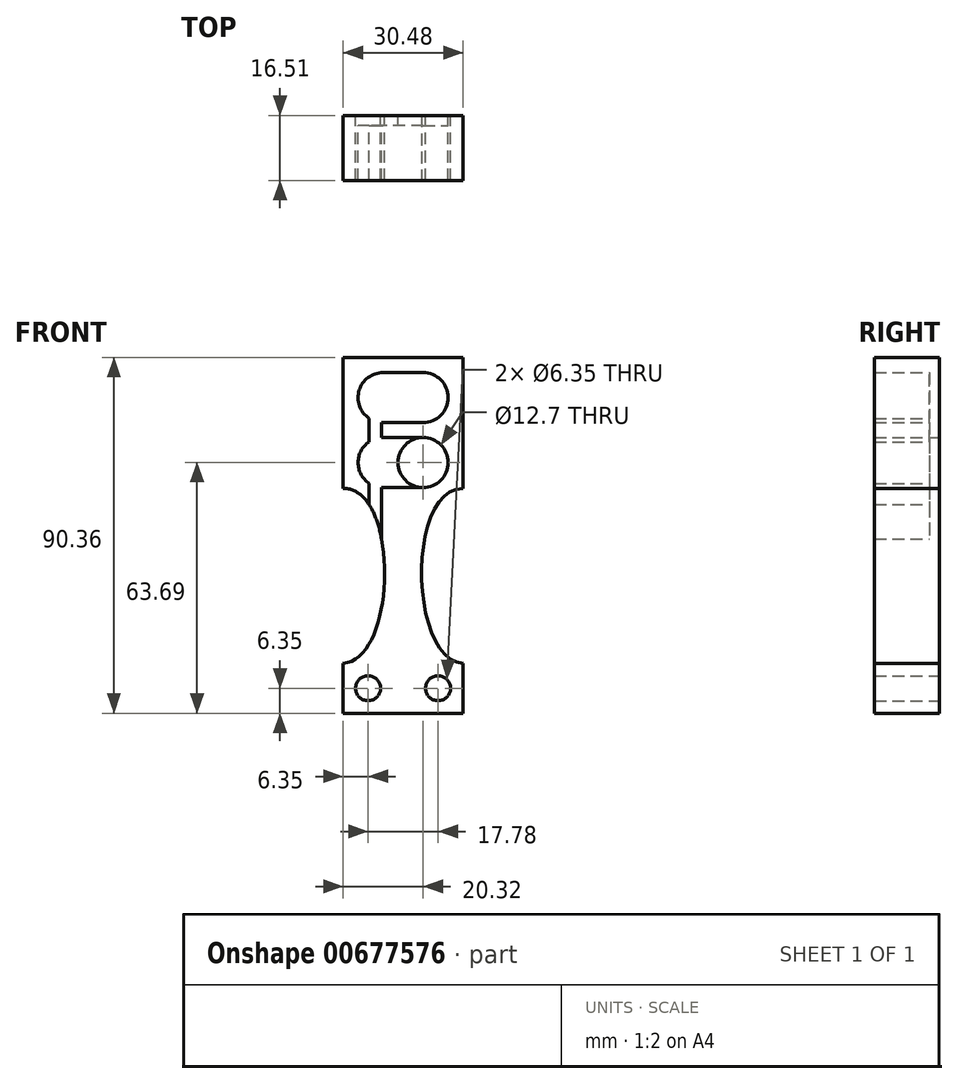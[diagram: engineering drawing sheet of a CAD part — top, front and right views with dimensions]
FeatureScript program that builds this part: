
annotation { "Feature Type Name" : "Feature", "Feature Type Description" : "" }
export const myFeature = defineFeature(function(context is Context, id is Id, definition is map)
    precondition{}
    {
        {
            var Q0;
            Q0=qCreatedBy(makeId("Front.planeOp"),FACE);
            var sketch = newSketch(context, id + "F0", { "sketchPlane" : qUnion([Q0])});
            skLineSegment(sketch, "E0", {"start": v(0, 10.16) * mm, "end": v(15.24, 10.16) * mm});
            skLineSegment(sketch, "E1", {"start": v(15.24, 10.16) * mm, "end": v(15.24, -23.05) * mm});
            skLineSegment(sketch, "E2", {"start": v(37.3, -67.5) * mm, "end": v(37.3, -80.2) * mm});
            skLineSegment(sketch, "E3", {"start": v(37.3, -80.2) * mm, "end": v(0, -80.2) * mm});
            skLineSegment(sketch, "E4.MirrorCS", {"start": v(-15.24, 10.16) * mm, "end": v(-15.24, -23.05) * mm});
            skLineSegment(sketch, "E5.MirrorCS", {"start": v(-37.3, -67.5) * mm, "end": v(-37.3, -80.2) * mm});
            skLineSegment(sketch, "E6.MirrorCS", {"start": v(0, 10.16) * mm, "end": v(-15.24, 10.16) * mm});
            skLineSegment(sketch, "E7.MirrorCS", {"start": v(-37.3, -80.2) * mm, "end": v(0, -80.2) * mm});
            skLineSegment(sketch, "E8", {"start": v(-37.3, -67.5) * mm, "end": v(-15.24, -67.5) * mm});
            skLineSegment(sketch, "E9.MirrorCS", {"start": v(37.3, -67.5) * mm, "end": v(15.24, -67.5) * mm});
            skCircle(sketch, "E10", {"center": v(5.08, 0) * mm, "radius": 6.35 * mm});
            skCircle(sketch, "E11.MirrorC", {"center": v(-5.08, 0) * mm, "radius": 6.35 * mm});
            skLineSegment(sketch, "E12", {"start": v(5.08, 6.35) * mm, "end": v(-5.08, 6.35) * mm});
            skLineSegment(sketch, "E13", {"start": v(-5.08, -6.35) * mm, "end": v(5.08, -6.35) * mm});
            skFitSpline(sketch, "E14", {"points": [v(-15.24, -23.05) * mm, v(-15.24, -67.5) * mm], "startDerivative": vector(43.33, 0) * mm, "endDerivative": vector(-41, -2.46) * mm});
            skFitSpline(sketch, "E15.MirrorCS", {"points": [v(15.24, -23.05) * mm, v(15.24, -67.5) * mm], "startDerivative": vector(-43.33, 0) * mm, "endDerivative": vector(41, -2.46) * mm});
            skCircle(sketch, "E16", {"center": v(-5.08, -16.51) * mm, "radius": 6.35 * mm});
            skCircle(sketch, "E17.MirrorC", {"center": v(5.08, -16.51) * mm, "radius": 6.35 * mm});
            skLineSegment(sketch, "E18", {"start": v(5.08, -10.16) * mm, "end": v(-5.08, -10.16) * mm});
            skLineSegment(sketch, "E19", {"start": v(5.08, -22.86) * mm, "end": v(-5.08, -22.86) * mm});
            skPoint(sketch, "E20", {"position": v(0, -16.51) * mm});
            skLineSegment(sketch, "E21", {"start": v(-8.64, -21.77) * mm, "end": v(-8.64, -27.19) * mm});
            skLineSegment(sketch, "E22", {"start": v(-5.46, -6.34) * mm, "end": v(-5.46, -10.17) * mm});
            skLineSegment(sketch, "E23", {"start": v(-5.46, -10.17) * mm, "end": v(-5.46, -22.6) * mm});
            skLineSegment(sketch, "E24", {"start": v(-5.46, -22.6) * mm, "end": v(-5.46, -35.93) * mm});
            skLineSegment(sketch, "E25", {"start": v(-15.24, -67.5) * mm, "end": v(-15.24, -80.2) * mm});
            skPoint(sketch, "E25.endSnap0", {"position": v(-18.65, -80.2) * mm});
            skLineSegment(sketch, "E26", {"start": v(15.24, -67.5) * mm, "end": v(15.24, -80.2) * mm});
            skLineSegment(sketch, "E27", {"start": v(-8.64, -11.25) * mm, "end": v(-8.64, -5.26) * mm});
            skCircle(sketch, "E28", {"center": v(8.89, -73.85) * mm, "radius": 3.18 * mm});
            skCircle(sketch, "E29.MirrorC", {"center": v(-8.89, -73.85) * mm, "radius": 3.18 * mm});
            skSolve(sketch);
        }
        {
            var Q0;
            Q0=makeQuery(id+"F0.imprint","IMPRINT",FACE,{"disambiguationData":[TD([[makeQuery(id+"F0.imprint","IMPRINT",EDGE,{"derivedFrom":sQuery(id+"F0.wireOp",EDGE,"E0")}),-1.0]])]});
            extrude(context, id + "F1", {"entities" : qUnion([Q0]), "depth" : 16.5 * mm, "offsetDistance" : 25.4 * mm});
        }
        {
            var Q0;
            {var subQ0=sQuery(id+"F0.wireOp",EDGE,"E11.MirrorC");var subQ2=sQuery(id+"F0.wireOp",EDGE,"E10");var subQ5=makeQuery(id+"F0.imprint","INTERSECT",VERTEX,{"disambiguationData":[OD(0.0)],"derivedFrom":[subQ2,subQ0]});Q0=makeQuery(id+"F0.imprint","IMPRINT",FACE,{"disambiguationData":[TD([[makeQuery(id+"F0.imprint","IMPRINT",EDGE,{"disambiguationData":[TD([[subQ5,-1.0]])],"derivedFrom":subQ2}),-1.0]])]});}
            var Q1;
            {var subQ0=sQuery(id+"F0.wireOp",EDGE,"E10");var subQ1=makeQuery(id+"F0.imprint","INTERSECT",VERTEX,{"derivedFrom":[subQ0,sQuery(id+"F0.wireOp",EDGE,"E12")]});Q1=makeQuery(id+"F0.imprint","IMPRINT",FACE,{"disambiguationData":[TD([[makeQuery(id+"F0.imprint","IMPRINT",EDGE,{"disambiguationData":[TD([[subQ1,-1.0]])],"derivedFrom":subQ0}),1.0]])]});}
            var Q2;
            {var subQ0=sQuery(id+"F0.wireOp",EDGE,"E12");Q2=makeQuery(id+"F0.imprint","IMPRINT",FACE,{"disambiguationData":[TD([[makeQuery(id+"F0.imprint","IMPRINT",EDGE,{"derivedFrom":subQ0}),1.0]])]});}
            var Q3;
            {var subQ0=sQuery(id+"F0.wireOp",EDGE,"E11.MirrorC");var subQ1=sQuery(id+"F0.wireOp",EDGE,"E10");var subQ2=makeQuery(id+"F0.imprint","INTERSECT",VERTEX,{"disambiguationData":[OD(0.0)],"derivedFrom":[subQ1,subQ0]});Q3=makeQuery(id+"F0.imprint","IMPRINT",FACE,{"disambiguationData":[TD([[makeQuery(id+"F0.imprint","IMPRINT",EDGE,{"disambiguationData":[TD([[subQ2,-1.0]])],"derivedFrom":subQ1}),1.0]])]});}
            var Q4;
            {var subQ0=sQuery(id+"F0.wireOp",EDGE,"E13");Q4=makeQuery(id+"F0.imprint","IMPRINT",FACE,{"disambiguationData":[TD([[makeQuery(id+"F0.imprint","IMPRINT",EDGE,{"derivedFrom":subQ0}),1.0]])]});}
            var Q5;
            {var subQ0=sQuery(id+"F0.wireOp",EDGE,"E16");var subQ4=makeQuery(id+"F0.imprint","INTERSECT",VERTEX,{"derivedFrom":[subQ0,sQuery(id+"F0.wireOp",EDGE,"E18")]});Q5=makeQuery(id+"F0.imprint","IMPRINT",FACE,{"disambiguationData":[TD([[makeQuery(id+"F0.imprint","IMPRINT",EDGE,{"disambiguationData":[TD([[subQ4,1.0]])],"derivedFrom":subQ0}),1.0]])]});}
            var Q6;
            {var subQ0=sQuery(id+"F0.wireOp",EDGE,"E16");var subQ2=sQuery(id+"F0.wireOp",EDGE,"E23");var subQ4=makeQuery(id+"F0.imprint","INTERSECT",VERTEX,{"derivedFrom":[subQ0,subQ2]});Q6=makeQuery(id+"F0.imprint","IMPRINT",FACE,{"disambiguationData":[TD([[makeQuery(id+"F0.imprint","IMPRINT",EDGE,{"disambiguationData":[TD([[subQ4,1.0]])],"derivedFrom":subQ0}),1.0]])]});}
            var Q7;
            {var subQ0=sQuery(id+"F0.wireOp",EDGE,"E17.MirrorC");var subQ1=sQuery(id+"F0.wireOp",EDGE,"E16");var subQ2=makeQuery(id+"F0.imprint","INTERSECT",VERTEX,{"disambiguationData":[OD(0.0)],"derivedFrom":[subQ1,subQ0]});Q7=makeQuery(id+"F0.imprint","IMPRINT",FACE,{"disambiguationData":[TD([[makeQuery(id+"F0.imprint","IMPRINT",EDGE,{"disambiguationData":[TD([[subQ2,1.0]])],"derivedFrom":subQ1}),1.0]])]});}
            var Q8;
            {var subQ0=sQuery(id+"F0.wireOp",EDGE,"E18");Q8=makeQuery(id+"F0.imprint","IMPRINT",FACE,{"disambiguationData":[TD([[makeQuery(id+"F0.imprint","IMPRINT",EDGE,{"derivedFrom":subQ0}),1.0]])]});}
            var Q9;
            {var subQ0=sQuery(id+"F0.wireOp",EDGE,"E17.MirrorC");var subQ1=sQuery(id+"F0.wireOp",EDGE,"E16");var subQ2=makeQuery(id+"F0.imprint","INTERSECT",VERTEX,{"disambiguationData":[OD(0.0)],"derivedFrom":[subQ1,subQ0]});Q9=makeQuery(id+"F0.imprint","IMPRINT",FACE,{"disambiguationData":[TD([[makeQuery(id+"F0.imprint","IMPRINT",EDGE,{"disambiguationData":[TD([[subQ2,1.0]])],"derivedFrom":subQ1}),-1.0]])]});}
            var Q10;
            {var subQ0=sQuery(id+"F0.wireOp",EDGE,"E19");Q10=makeQuery(id+"F0.imprint","IMPRINT",FACE,{"disambiguationData":[TD([[makeQuery(id+"F0.imprint","IMPRINT",EDGE,{"derivedFrom":subQ0}),-1.0]])]});}
            var Q11;
            {var subQ0=sQuery(id+"F0.wireOp",EDGE,"3nQBnrxE-CDFu-dkHD-LFef-8Zr9rkai0jz6");Q11=makeQuery(id+"F0.imprint","IMPRINT",FACE,{"disambiguationData":[TD([[makeQuery(id+"F0.imprint","IMPRINT",EDGE,{"derivedFrom":subQ0}),1.0]])]});}
            var Q12;
            {var subQ0=sQuery(id+"F0.wireOp",EDGE,"E21");Q12=makeQuery(id+"F0.imprint","IMPRINT",FACE,{"disambiguationData":[TD([[makeQuery(id+"F0.imprint","IMPRINT",EDGE,{"derivedFrom":subQ0}),1.0]])]});}
            var Q13;
            {var subQ0=sQuery(id+"F0.wireOp",EDGE,"E22");Q13=makeQuery(id+"F0.imprint","IMPRINT",FACE,{"disambiguationData":[TD([[makeQuery(id+"F0.imprint","IMPRINT",EDGE,{"derivedFrom":subQ0}),-1.0]])]});}
            var Q14;
            {var subQ0=sQuery(id+"F0.wireOp",EDGE,"E23");Q14=makeQuery(id+"F0.imprint","IMPRINT",FACE,{"disambiguationData":[TD([[makeQuery(id+"F0.imprint","IMPRINT",EDGE,{"derivedFrom":subQ0}),-1.0]])]});}
            extrude(context, id + "F2", {"entities" : qUnion([Q0, Q1, Q2, Q3, Q4, Q5, Q6, Q7, Q8, Q9, Q10, Q11, Q12, Q13, Q14]), "operationType" : NewBodyOperationType.ADD, "depth" : 2.54 * mm, "offsetDistance" : 25.4 * mm});
        }
    });
